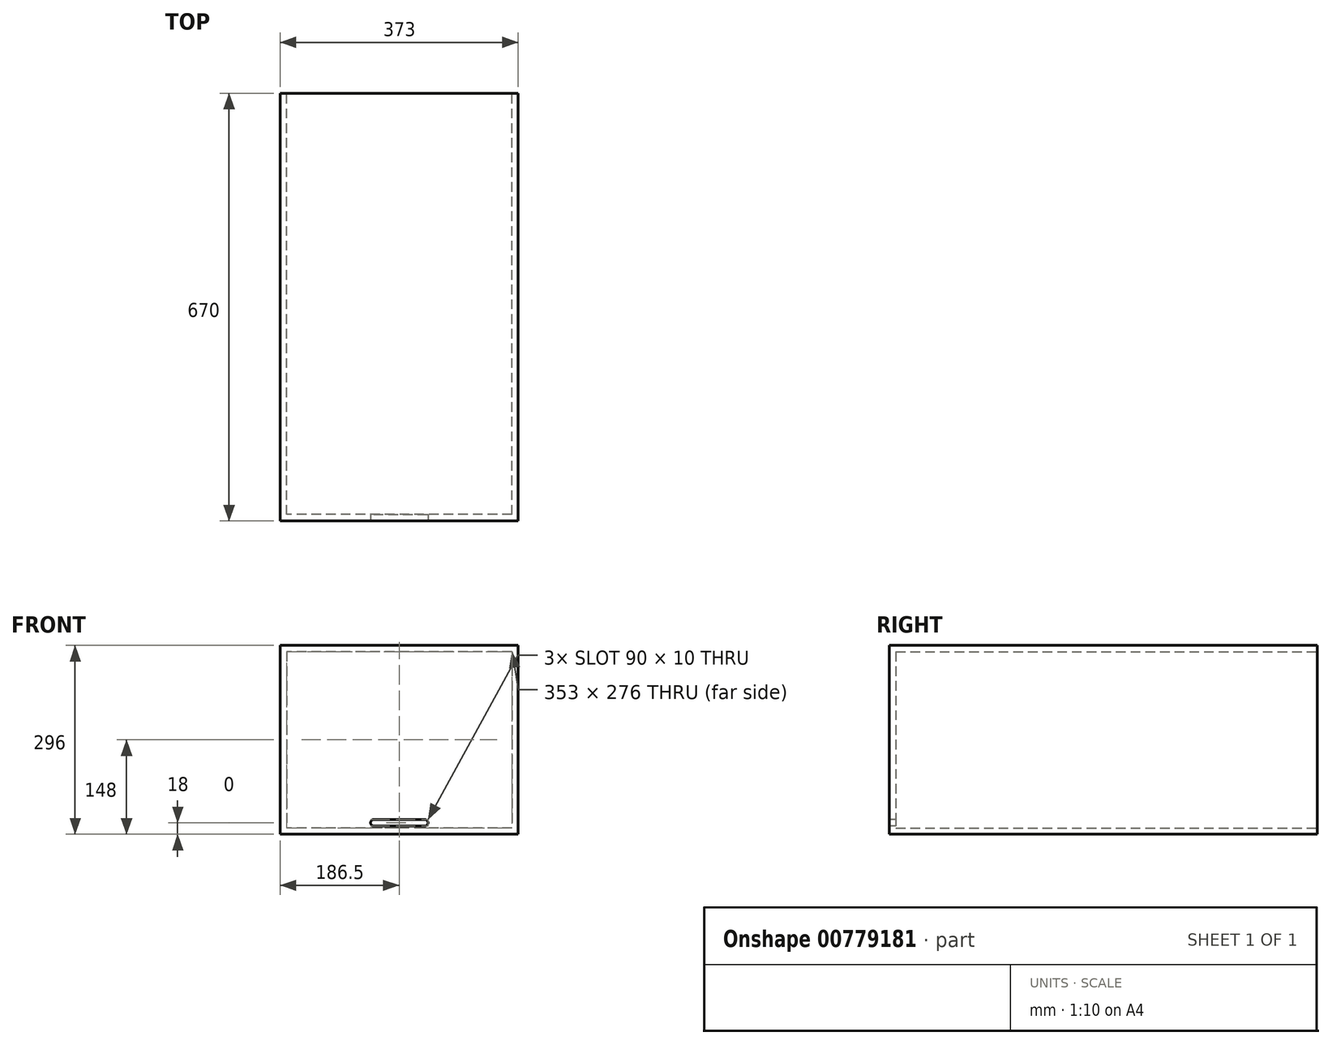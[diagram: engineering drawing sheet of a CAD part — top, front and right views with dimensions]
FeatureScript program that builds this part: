
annotation { "Feature Type Name" : "Feature", "Feature Type Description" : "" }
export const myFeature = defineFeature(function(context is Context, id is Id, definition is map)
    precondition{}
    {
        {
            var Q0;
            Q0=qCreatedBy(makeId("Front.planeOp"),FACE);
            var sketch = newSketch(context, id + "F0", { "sketchPlane" : qUnion([Q0])});
            skLineSegment(sketch, "E0.bottom", {"start": v(186.5, 148) * mm, "end": v(-186.5, 148) * mm});
            skLineSegment(sketch, "E0.top", {"start": v(186.5, -148) * mm, "end": v(-186.5, -148) * mm});
            skLineSegment(sketch, "E0.left", {"start": v(186.5, 148) * mm, "end": v(186.5, -148) * mm});
            skLineSegment(sketch, "E0.right", {"start": v(-186.5, 148) * mm, "end": v(-186.5, -148) * mm});
            skPoint(sketch, "E0.middle", {"position": v(0, 0) * mm});
            skSolve(sketch);
        }
        {
            var Q0;
            Q0 = qSketchRegion(id + "F0", true);
            extrude(context, id + "F1", {"entities" : qUnion([Q0]), "depth" : 670 * mm, "offsetDistance" : 25 * mm});
        }
        {
            var Q0;
            Q0=makeQuery(id+"F1.opExtrude","CAP_FACE",FACE,{"disambiguationData":[OSD([sQuery(id+"F0.wireOp",EDGE,"E0.bottom"),sQuery(id+"F0.wireOp",EDGE,"E0.top"),sQuery(id+"F0.wireOp",EDGE,"E0.left"),sQuery(id+"F0.wireOp",EDGE,"E0.right")])],"isStart":true});
            shell(context, id + "F2", {"entities" : qUnion([Q0]), "thickness" : 10 * mm});
        }
        {
            var Q0;
            Q0=makeQuery(id+"F1.opExtrude","CAP_FACE",FACE,{"disambiguationData":[OSD([sQuery(id+"F0.wireOp",EDGE,"E0.bottom"),sQuery(id+"F0.wireOp",EDGE,"E0.top"),sQuery(id+"F0.wireOp",EDGE,"E0.left"),sQuery(id+"F0.wireOp",EDGE,"E0.right")])],"isStart":false});
            var sketch = newSketch(context, id + "F3", { "sketchPlane" : qUnion([Q0])});
            skLineSegment(sketch, "E1", {"start": v(-40, -130) * mm, "end": v(40, -130) * mm});
            skArc(sketch, "E2.0.startCap", {"start": v(-40, -135) * mm, "mid": v(-45, -130) * mm, "end": v(-40, -125) * mm});
            skArc(sketch, "E2.0.endCap", {"start": v(40, -125) * mm, "mid": v(45, -130) * mm, "end": v(40, -135) * mm});
            skLineSegment(sketch, "E2.0.left", {"start": v(-40, -125) * mm, "end": v(40, -125) * mm});
            skLineSegment(sketch, "E2.0.right", {"start": v(-40, -135) * mm, "end": v(40, -135) * mm});
            skSolve(sketch);
        }
        {
            var Q0;
            Q0 = qSketchRegion(id + "F3", true);
            extrude(context, id + "F4", {"entities" : qUnion([Q0]), "operationType" : NewBodyOperationType.REMOVE, "oppositeDirection" : true, "depth" : 25 * mm, "offsetDistance" : 25 * mm});
        }
    });
